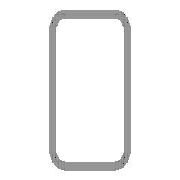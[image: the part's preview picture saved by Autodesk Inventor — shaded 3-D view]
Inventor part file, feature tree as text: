
AUTODESK INVENTOR PART (.ipt)
format: ipt  version: 2025 (Build 290162010, 162A)  size: 133,120 bytes
history: native  units: mm (DEFAULTED — no unit token found)
features: other x4, sketch x1, plane x1
ambient origin geometry x8: Origin, YZ Plane, XZ Plane, XY Plane, X Axis, Y Axis, Z Axis, Center Point
bodies: Solid1 (feature_tree), Body (feature_tree)
feature tree (6):
  parser-record x1  (decoder bookkeeping rows leaked as tree rows — omitted from the tree; the rows remain in map.json)
  other  "Driven Length"
  other  "Start Plane"
  other  "End Plane"
  sketch  "Sketch3"  dims[d3=2600.0mm d4=0.0mm d7=4.0mm d9=40.0mm d11=60.0mm d12=2.0mm d13=-0.0mm d14=2600.0mm d15=20.0mm d16=30.0mm d17=90.0deg d18=2600.0mm]
  plane  "Work Plane3"
